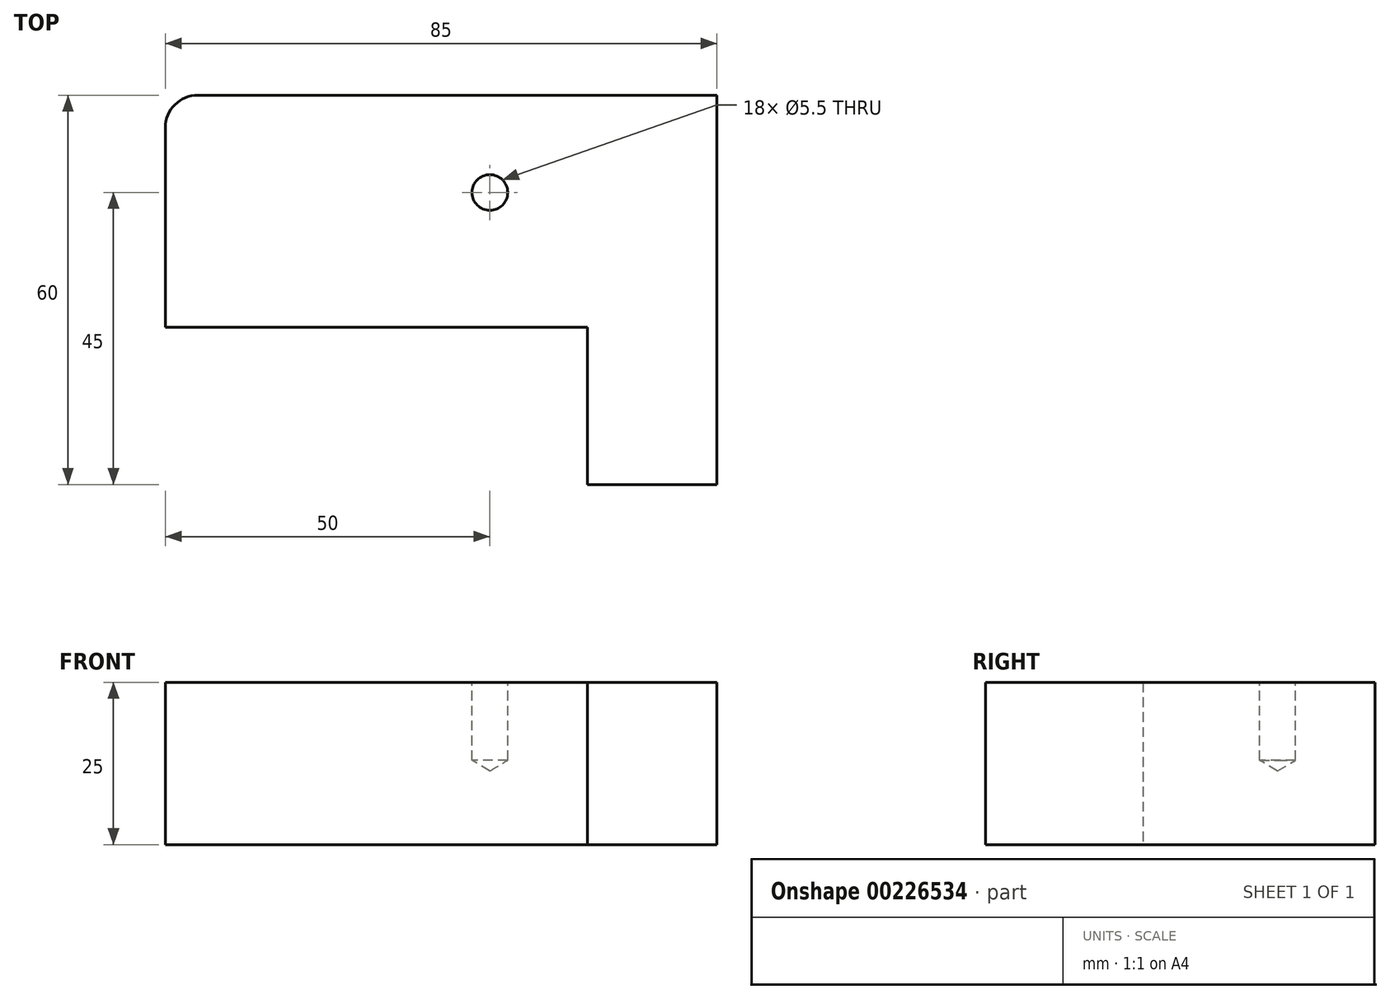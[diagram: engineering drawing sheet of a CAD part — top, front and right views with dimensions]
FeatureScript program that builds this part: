
annotation { "Feature Type Name" : "Feature", "Feature Type Description" : "" }
export const myFeature = defineFeature(function(context is Context, id is Id, definition is map)
    precondition{}
    {
        {
            var Q0;
            Q0=qCreatedBy(makeId("Top.planeOp"),FACE);
            var sketch = newSketch(context, id + "F0", { "sketchPlane" : qUnion([Q0])});
            skLineSegment(sketch, "E0", {"start": v(-60, 35.75) * mm, "end": v(20, 35.75) * mm});
            skLineSegment(sketch, "E1", {"start": v(20, 35.75) * mm, "end": v(20, -24.25) * mm});
            skLineSegment(sketch, "E2", {"start": v(20, -24.25) * mm, "end": v(0, -24.25) * mm});
            skLineSegment(sketch, "E3", {"start": v(0, -24.25) * mm, "end": v(0, 0) * mm});
            skLineSegment(sketch, "E4", {"start": v(0, 0) * mm, "end": v(-65, 0) * mm});
            skLineSegment(sketch, "E5", {"start": v(-65, 0) * mm, "end": v(-65, 30.75) * mm});
            skPoint(sketch, "E6.visualSharp", {"position": v(-65, 35.75) * mm});
            skArc(sketch, "E6.filletArc", {"start": v(-60, 35.75) * mm, "mid": v(-63.54, 34.29) * mm, "end": v(-65, 30.75) * mm});
            skSolve(sketch);
        }
        {
            var Q0;
            Q0=makeQuery(id+"F0.imprint","IMPRINT",FACE,{"disambiguationData":[TD([[makeQuery(id+"F0.imprint","IMPRINT",EDGE,{"derivedFrom":sQuery(id+"F0.wireOp",EDGE,"E0")}),-1.0]])]});
            extrude(context, id + "F1", {"entities" : qUnion([Q0]), "depth" : 25 * mm});
        }
        {
            var Q0;
            Q0=makeQuery(id+"F1.opExtrude","CAP_FACE",FACE,{"disambiguationData":[OSD([sQuery(id+"F0.wireOp",EDGE,"E0"),sQuery(id+"F0.wireOp",EDGE,"E1"),sQuery(id+"F0.wireOp",EDGE,"E2"),sQuery(id+"F0.wireOp",EDGE,"E3"),sQuery(id+"F0.wireOp",EDGE,"E4"),sQuery(id+"F0.wireOp",EDGE,"E5"),sQuery(id+"F0.wireOp",EDGE,"E6.filletArc")])],"isStart":false});
            var sketch = newSketch(context, id + "F2", { "sketchPlane" : qUnion([Q0])});
            skPoint(sketch, "E7", {"position": v(-15, 20.75) * mm});
            skSolve(sketch);
        }
        {
            var Q0;
            Q0=sQuery(id+"F2.wireOp",VERTEX,"E7");
            var Q1;
            Q1=makeQuery(id+"F1.opExtrude","SWEPT_BODY",BODY,{"disambiguationData":[OSD([sQuery(id+"F0.wireOp",EDGE,"E0"),sQuery(id+"F0.wireOp",EDGE,"E1"),sQuery(id+"F0.wireOp",EDGE,"E2"),sQuery(id+"F0.wireOp",EDGE,"E3"),sQuery(id+"F0.wireOp",EDGE,"E4"),sQuery(id+"F0.wireOp",EDGE,"E5"),sQuery(id+"F0.wireOp",EDGE,"E6.filletArc")])]});
            hole(context, id + "F3", {"style" : HoleStyle.SIMPLE, "endStyle" : HoleEndStyle.BLIND, "standardTappedOrClearance" : lookupTablePath({ "standard" : "ISO", "fit" : "Normal", "size" : "M5", "type" : "Clearance" }), "standardBlindInLast" : lookupTablePath({ "fit" : "Standard", "standard" : "ISO", "size" : "M5", "type" : "Clearance" }), "holeDiameter" : 5.5 * mm, "holeDepth" : 12 * mm, "locations" : qUnion([Q0]), "scope" : qUnion([Q1])});
        }
    });
